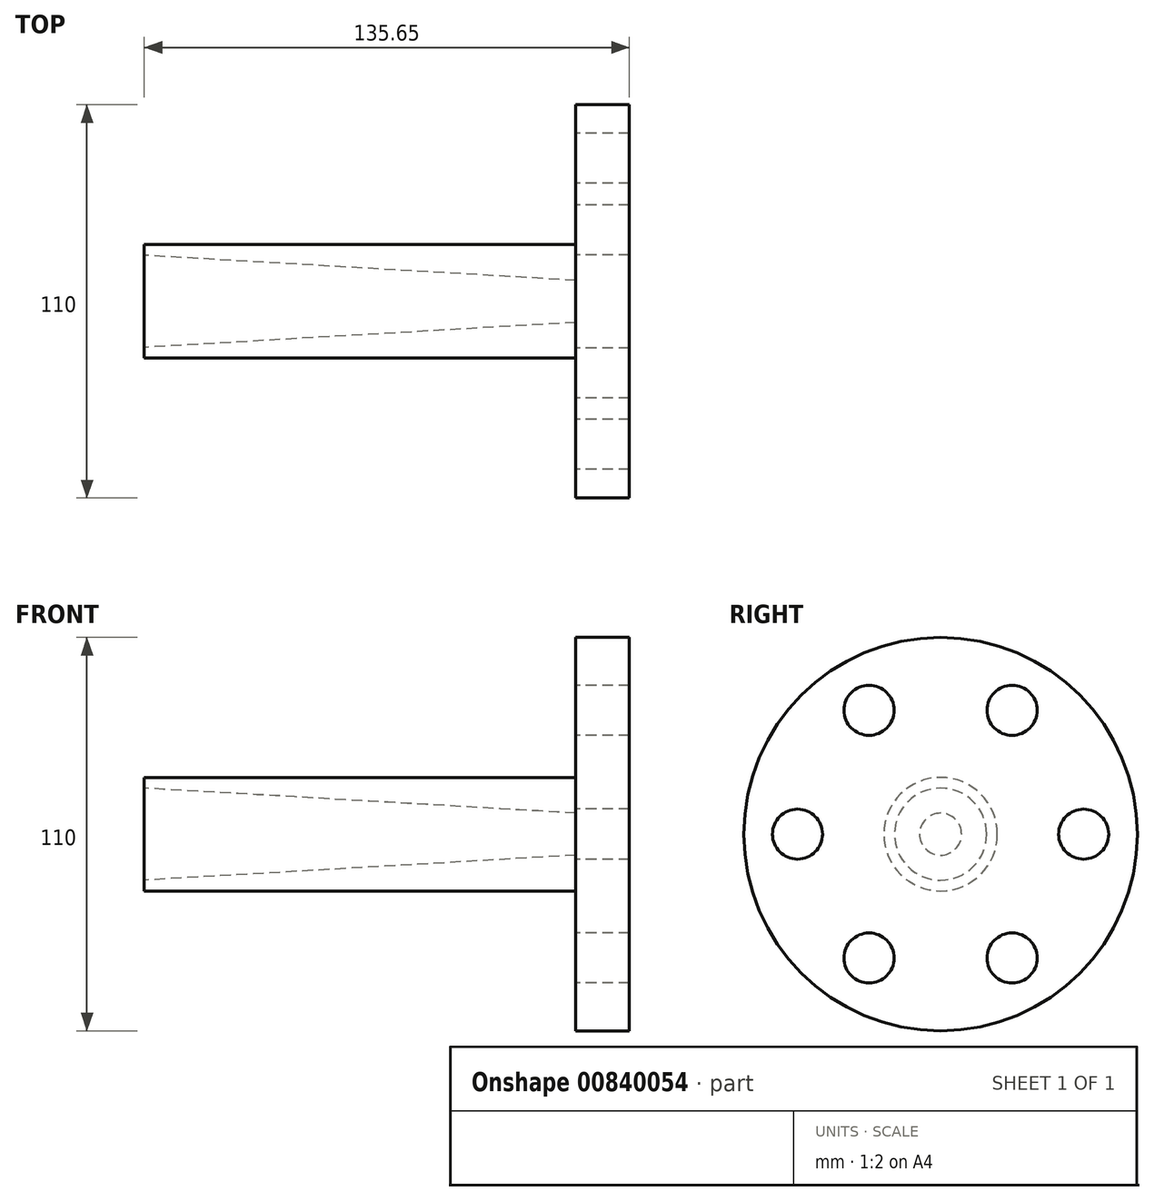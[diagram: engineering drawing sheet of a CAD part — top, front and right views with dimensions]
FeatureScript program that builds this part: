
annotation { "Feature Type Name" : "Feature", "Feature Type Description" : "" }
export const myFeature = defineFeature(function(context is Context, id is Id, definition is map)
    precondition{}
    {
        {
            var Q0;
            Q0=qCreatedBy(makeId("Front.planeOp"),FACE);
            var sketch = newSketch(context, id + "F0", { "sketchPlane" : qUnion([Q0])});
            skLineSegment(sketch, "E0", {"start": v(0, 0) * mm, "end": v(120.65, 0) * mm});
            skLineSegment(sketch, "E1", {"start": v(0, 12.88) * mm, "end": v(0, 15.88) * mm});
            skLineSegment(sketch, "E2", {"start": v(0, 15.88) * mm, "end": v(0, 15.88) * mm});
            skLineSegment(sketch, "E3", {"start": v(120.15, 36.17) * mm, "end": v(120.15, 36.17) * mm});
            skLineSegment(sketch, "E4", {"start": v(0, 15.88) * mm, "end": v(120.65, 15.88) * mm});
            skLineSegment(sketch, "E5", {"start": v(120.65, 15.88) * mm, "end": v(120.65, 0) * mm});
            skLineSegment(sketch, "E6", {"start": v(0, 12.88) * mm, "end": v(120.65, 5.88) * mm});
            skSolve(sketch);
        }
        {
            var Q0;
            Q0 = qSketchRegion(id + "F0", true);
            var Q1;
            Q1=sQuery(id+"F0.wireOp",EDGE,"E0");
            revolve(context, id + "F1", {"surfaceOperationType" : NewSurfaceOperationType.NEW, "entities" : qUnion([Q0]), "axis" : qUnion([Q1]), "revolveType" : RevolveType.FULL});
        }
        {
            var Q0;
            Q0=makeQuery(id+"F1.opRevolve","SWEPT_FACE",FACE,{"disambiguationData":[OSD([sQuery(id+"F0.wireOp",EDGE,"E5")])]});
            var sketch = newSketch(context, id + "F2", { "sketchPlane" : qUnion([Q0])});
            skCircle(sketch, "E7", {"center": v(0, 0) * mm, "radius": 55 * mm});
            skCircle(sketch, "E8", {"center": v(-40, 0) * mm, "radius": 7 * mm});
            skCircle(sketch, "E9.1.0", {"center": v(-20, 34.64) * mm, "radius": 7 * mm});
            skCircle(sketch, "E9.2.0", {"center": v(20, 34.64) * mm, "radius": 7 * mm});
            skLineSegment(sketch, "E9.anchor1", {"start": v(0, 0) * mm, "end": v(-40, 0) * mm, "construction": true});
            skLineSegment(sketch, "E9.anchor2", {"start": v(0, 0) * mm, "end": v(-20, -34.64) * mm, "construction": true});
            skCircle(sketch, "E10.1.3.0", {"center": v(40, 0) * mm, "radius": 7 * mm});
            skCircle(sketch, "E10.1.4.0", {"center": v(20, -34.64) * mm, "radius": 7 * mm});
            skCircle(sketch, "E10.1.5.0", {"center": v(-20, -34.64) * mm, "radius": 7 * mm});
            skSolve(sketch);
        }
        {
            var Q0;
            Q0 = qSketchRegion(id + "F2", true);
            extrude(context, id + "F3", {"entities" : qUnion([Q0]), "depth" : 15 * mm, "offsetDistance" : 25 * mm});
        }
    });
